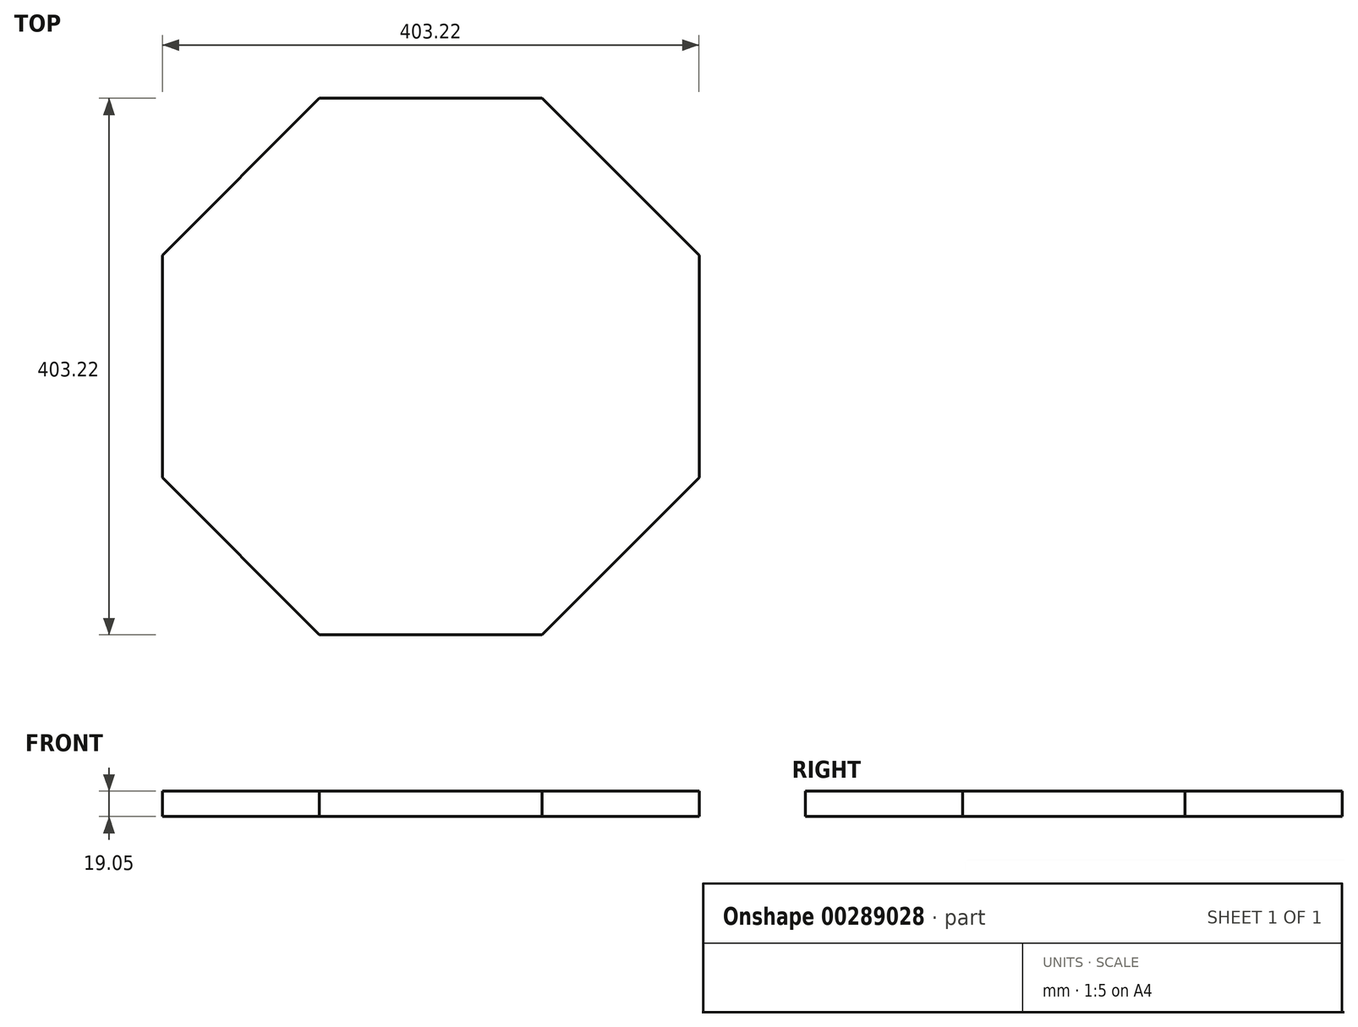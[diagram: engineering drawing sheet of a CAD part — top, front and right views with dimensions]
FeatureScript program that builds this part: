
annotation { "Feature Type Name" : "Feature", "Feature Type Description" : "" }
export const myFeature = defineFeature(function(context is Context, id is Id, definition is map)
    precondition{}
    {
        {
            var Q0;
            Q0=qCreatedBy(makeId("Top.planeOp"),FACE);
            var sketch = newSketch(context, id + "F0", { "sketchPlane" : qUnion([Q0])});
            skCircle(sketch, "E0.cCircle", {"center": v(0, 0) * mm, "radius": 201.61 * mm, "construction": true});
            skLineSegment(sketch, "E0.0", {"start": v(83.51, -201.61) * mm, "end": v(-83.51, -201.61) * mm});
            skLineSegment(sketch, "E0.1", {"start": v(-83.51, -201.61) * mm, "end": v(-201.61, -83.51) * mm});
            skLineSegment(sketch, "E0.2", {"start": v(-201.61, -83.51) * mm, "end": v(-201.61, 83.51) * mm});
            skLineSegment(sketch, "E0.3", {"start": v(-201.61, 83.51) * mm, "end": v(-83.51, 201.61) * mm});
            skLineSegment(sketch, "E0.4", {"start": v(-83.51, 201.61) * mm, "end": v(83.51, 201.61) * mm});
            skLineSegment(sketch, "E0.5", {"start": v(83.51, 201.61) * mm, "end": v(201.61, 83.51) * mm});
            skLineSegment(sketch, "E0.6", {"start": v(201.61, 83.51) * mm, "end": v(201.61, -83.51) * mm});
            skLineSegment(sketch, "E0.7", {"start": v(201.61, -83.51) * mm, "end": v(83.51, -201.61) * mm});
            skSolve(sketch);
        }
        {
            var Q0;
            {var subQ10=sQuery(id+"F0.wireOp",EDGE,"E0.1");Q0=makeQuery(id+"F0.imprint","IMPRINT",FACE,{"disambiguationData":[TD([[makeQuery(id+"F0.imprint","IMPRINT",EDGE,{"derivedFrom":subQ10}),-1.0]])]});}
            var Q1;
            Q1=makeQuery(id+"F0.imprint","IMPRINT",FACE,{"disambiguationData":[TD([[makeQuery(id+"F0.imprint","IMPRINT",EDGE,{"derivedFrom":sQuery(id+"F0.wireOp",EDGE,"cQB56Oj9-MVuE-15PN-6T9K-02pJKK2n8hkS.bottom")}),-1.0]])]});
            var Q2;
            Q2=makeQuery(id+"F0.imprint","IMPRINT",FACE,{"disambiguationData":[TD([[makeQuery(id+"F0.imprint","IMPRINT",EDGE,{"derivedFrom":sQuery(id+"F0.wireOp",EDGE,"9uoT95YI-G5ih-k1UW-86AG-2Vm9nF5xw2fy.bottom")}),-1.0]])]});
            extrude(context, id + "F1", {"entities" : qUnion([Q0, Q1, Q2]), "depth" : 19.05 * mm});
        }
    });
